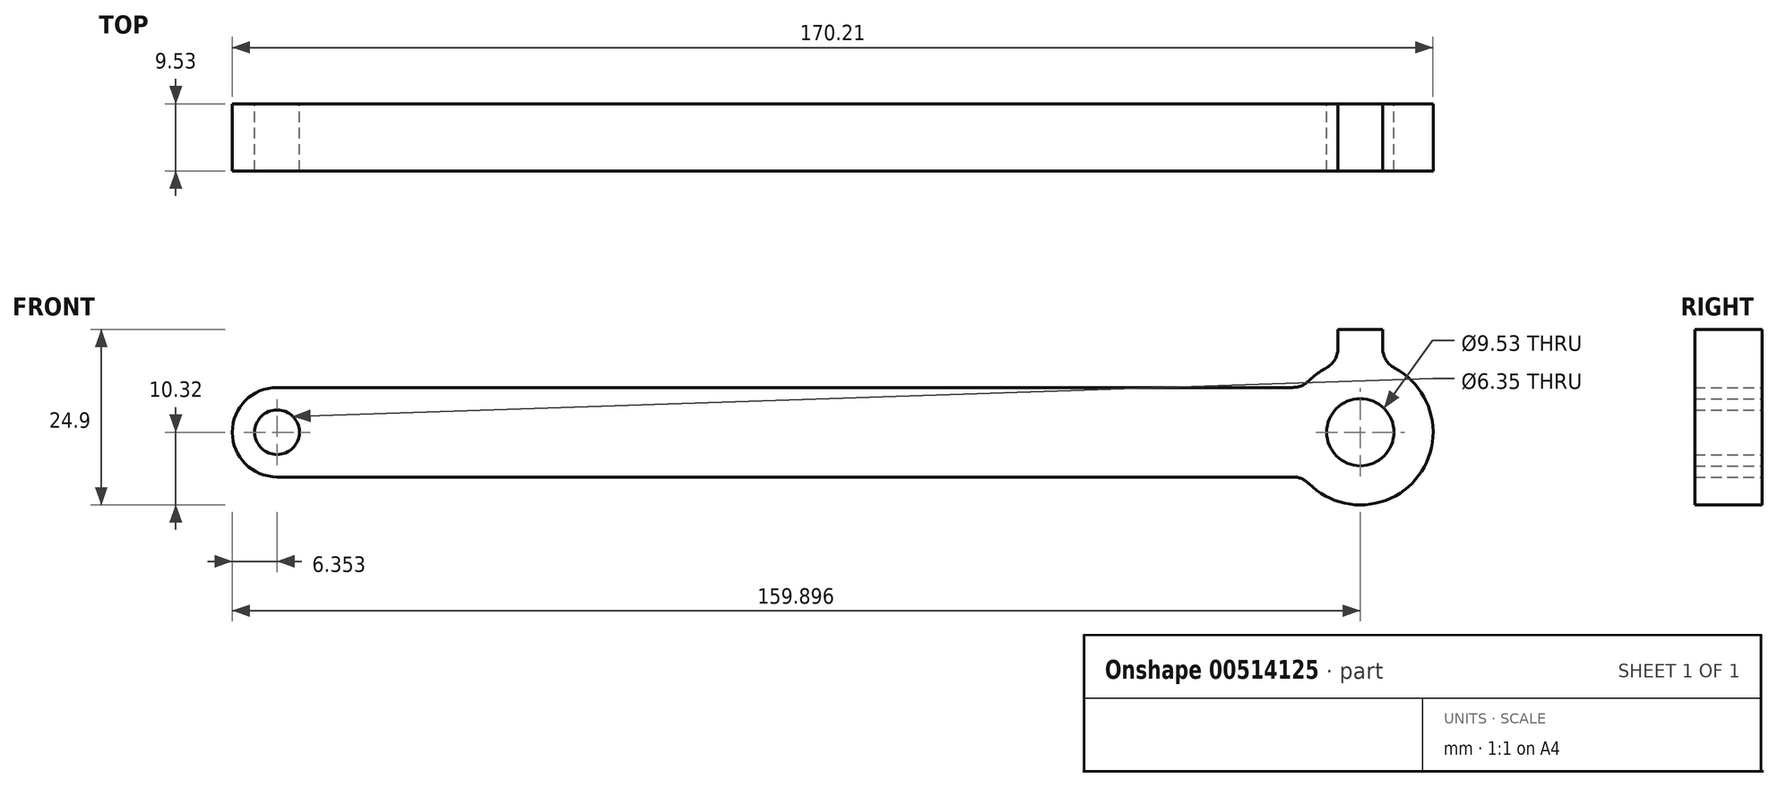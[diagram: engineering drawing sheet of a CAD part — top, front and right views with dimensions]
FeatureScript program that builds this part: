
annotation { "Feature Type Name" : "Feature", "Feature Type Description" : "" }
export const myFeature = defineFeature(function(context is Context, id is Id, definition is map)
    precondition{}
    {
        {
            var Q0;
            Q0=qCreatedBy(makeId("Front.planeOp"),FACE);
            var sketch = newSketch(context, id + "F0", { "sketchPlane" : qUnion([Q0])});
            skLineSegment(sketch, "E0", {"start": v(-174.84, 0) * mm, "end": v(209.27, 0) * mm, "construction": true});
            skLineSegment(sketch, "E1", {"start": v(-63.2, 45.74) * mm, "end": v(-63.2, -44.76) * mm, "construction": true});
            skLineSegment(sketch, "E2", {"start": v(90.35, 46.72) * mm, "end": v(90.35, -57.05) * mm, "construction": true});
            skCircle(sketch, "E3", {"center": v(-63.2, 0) * mm, "radius": 3.18 * mm});
            skCircle(sketch, "E4", {"center": v(-63.2, 0) * mm, "radius": 6.35 * mm});
            skCircle(sketch, "E5", {"center": v(90.35, 0) * mm, "radius": 10.32 * mm});
            skCircle(sketch, "E6", {"center": v(90.35, 0) * mm, "radius": 4.76 * mm});
            skLineSegment(sketch, "E7", {"start": v(-63.2, 6.35) * mm, "end": v(82.21, 6.35) * mm});
            skLineSegment(sketch, "E8", {"start": v(-63.2, -6.35) * mm, "end": v(82.21, -6.35) * mm});
            skLineSegment(sketch, "E9", {"start": v(93.52, 9.82) * mm, "end": v(93.52, 14.58) * mm});
            skLineSegment(sketch, "E10.MirrorCS", {"start": v(87.17, 9.82) * mm, "end": v(87.17, 14.58) * mm});
            skLineSegment(sketch, "E11", {"start": v(87.17, 14.58) * mm, "end": v(93.52, 14.58) * mm});
            skSolve(sketch);
        }
        {
            var Q0;
            {var subQ0=sQuery(id+"F0.wireOp",EDGE,"E7");Q0=makeQuery(id+"F0.imprint","IMPRINT",FACE,{"disambiguationData":[TD([[makeQuery(id+"F0.imprint","IMPRINT",EDGE,{"derivedFrom":subQ0}),-1.0]])]});}
            var Q1;
            Q1=makeQuery(id+"F0.imprint","IMPRINT",FACE,{"disambiguationData":[TD([[makeQuery(id+"F0.imprint","IMPRINT",EDGE,{"derivedFrom":sQuery(id+"F0.wireOp",EDGE,"E3")}),-1.0]])]});
            var Q2;
            Q2=makeQuery(id+"F0.imprint","IMPRINT",FACE,{"disambiguationData":[TD([[makeQuery(id+"F0.imprint","IMPRINT",EDGE,{"derivedFrom":sQuery(id+"F0.wireOp",EDGE,"E6")}),-1.0]])]});
            var Q3;
            {var subQ0=sQuery(id+"F0.wireOp",EDGE,"E9");Q3=makeQuery(id+"F0.imprint","IMPRINT",FACE,{"disambiguationData":[TD([[makeQuery(id+"F0.imprint","IMPRINT",EDGE,{"derivedFrom":subQ0}),1.0]])]});}
            extrude(context, id + "F1", {"entities" : qUnion([Q0, Q1, Q2, Q3]), "depth" : 9.52 * mm, "offsetDistance" : 25.4 * mm});
        }
        {
            var Q0;
            Q0=makeQuery(id+"F1.opExtrude","SWEPT_EDGE",EDGE,{"disambiguationData":[OSD([sQuery(id+"F0.wireOp",EDGE,"E5"),sQuery(id+"F0.wireOp",EDGE,"E7")])]});
            var Q1;
            Q1=makeQuery(id+"F1.opExtrude","SWEPT_EDGE",EDGE,{"disambiguationData":[OSD([sQuery(id+"F0.wireOp",EDGE,"E5"),sQuery(id+"F0.wireOp",EDGE,"E10.MirrorCS")])]});
            var Q2;
            Q2=makeQuery(id+"F1.opExtrude","SWEPT_EDGE",EDGE,{"disambiguationData":[OSD([sQuery(id+"F0.wireOp",EDGE,"E5"),sQuery(id+"F0.wireOp",EDGE,"E9")])]});
            var Q3;
            Q3=makeQuery(id+"F1.opExtrude","SWEPT_EDGE",EDGE,{"disambiguationData":[OSD([sQuery(id+"F0.wireOp",EDGE,"E5"),sQuery(id+"F0.wireOp",EDGE,"E8")])]});
            fillet(context, id + "F2", {"entities" : qUnion([Q0, Q1, Q2, Q3]), "tangentPropagation" : true, "radius" : 3.17 * mm, "defaultsChanged" : false, "vertexSettings" : [], "allowEdgeOverflow" : false});
        }
    });
